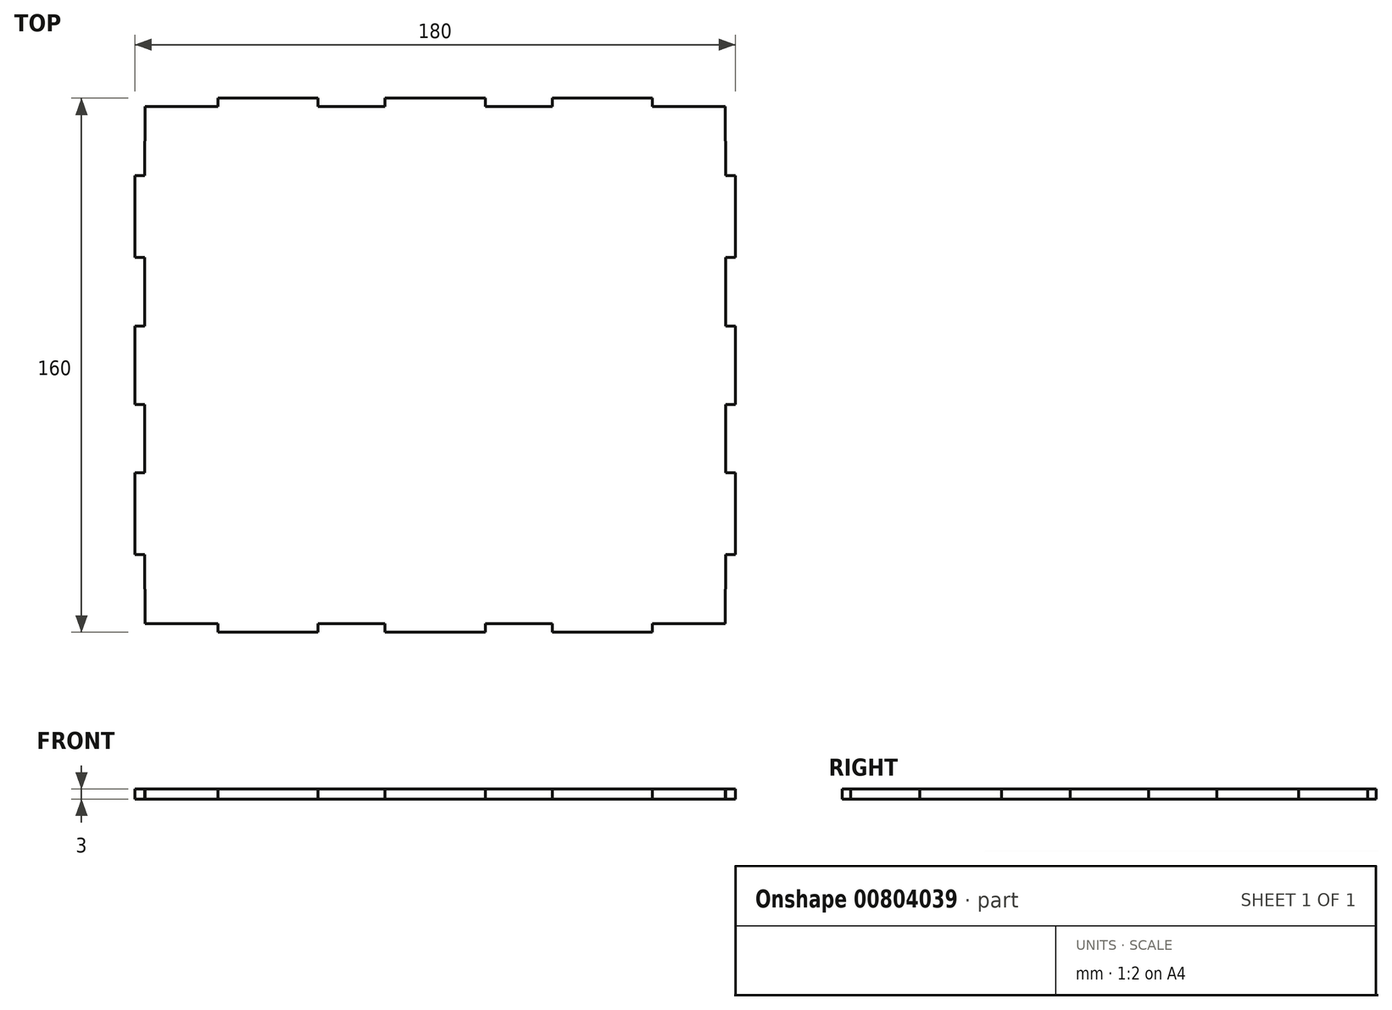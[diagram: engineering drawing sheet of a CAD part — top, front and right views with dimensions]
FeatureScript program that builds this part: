
annotation { "Feature Type Name" : "Feature", "Feature Type Description" : "" }
export const myFeature = defineFeature(function(context is Context, id is Id, definition is map)
    precondition{}
    {
        {
            var Q0;
            Q0=qCreatedBy(makeId("Top.planeOp"),FACE);
            var sketch = newSketch(context, id + "F0", { "sketchPlane" : qUnion([Q0])});
            skPoint(sketch, "E0.middle", {"position": v(0, 0) * mm});
            skLineSegment(sketch, "E1", {"start": v(90, 44.5) * mm, "end": v(88.5, 44.5) * mm});
            skLineSegment(sketch, "E2.bottom", {"start": v(87, 56.75) * mm, "end": v(90, 56.75) * mm});
            skLineSegment(sketch, "E2.top", {"start": v(87, 32.25) * mm, "end": v(90, 32.25) * mm});
            skLineSegment(sketch, "E2.right", {"start": v(90, 56.75) * mm, "end": v(90, 32.25) * mm});
            skPoint(sketch, "E2.middle", {"position": v(88.5, 44.5) * mm});
            skLineSegment(sketch, "E3.MirrorCS", {"start": v(87, -56.75) * mm, "end": v(90, -56.75) * mm});
            skLineSegment(sketch, "E4.MirrorCS", {"start": v(90, -56.75) * mm, "end": v(90, -32.25) * mm});
            skLineSegment(sketch, "E5.MirrorCS", {"start": v(87, -32.25) * mm, "end": v(90, -32.25) * mm});
            skLineSegment(sketch, "E6.bottom", {"start": v(90, 32.25) * mm, "end": v(87, 32.25) * mm});
            skLineSegment(sketch, "E6.top", {"start": v(90, 11.75) * mm, "end": v(87, 11.75) * mm});
            skLineSegment(sketch, "E6.right", {"start": v(87, 32.25) * mm, "end": v(87, 11.75) * mm});
            skPoint(sketch, "E6.middle", {"position": v(88.5, 22) * mm});
            skLineSegment(sketch, "E7.MirrorCS", {"start": v(87, -32.25) * mm, "end": v(87, -11.75) * mm});
            skLineSegment(sketch, "E8.MirrorCS", {"start": v(90, -11.75) * mm, "end": v(87, -11.75) * mm});
            skLineSegment(sketch, "E9", {"start": v(90, 11.75) * mm, "end": v(90, -11.75) * mm});
            skLineSegment(sketch, "E10.MirrorCS", {"start": v(-90, 32.25) * mm, "end": v(-87, 32.25) * mm});
            skLineSegment(sketch, "E11.MirrorCS", {"start": v(-87, 32.25) * mm, "end": v(-90, 32.25) * mm});
            skLineSegment(sketch, "E12.MirrorCS", {"start": v(-87, -56.75) * mm, "end": v(-90, -56.75) * mm});
            skLineSegment(sketch, "E13.MirrorCS", {"start": v(-87, -32.25) * mm, "end": v(-90, -32.25) * mm});
            skLineSegment(sketch, "E14.MirrorCS", {"start": v(-90, -11.75) * mm, "end": v(-87, -11.75) * mm});
            skLineSegment(sketch, "E15.MirrorCS", {"start": v(-87, 56.75) * mm, "end": v(-90, 56.75) * mm});
            skLineSegment(sketch, "E16.MirrorCS", {"start": v(-90, 44.5) * mm, "end": v(-88.5, 44.5) * mm});
            skLineSegment(sketch, "E17.MirrorCS", {"start": v(-90, 11.75) * mm, "end": v(-87, 11.75) * mm});
            skPoint(sketch, "E18.MirrorP", {"position": v(-88.5, 44.5) * mm});
            skLineSegment(sketch, "E19.MirrorCS", {"start": v(-90, 11.75) * mm, "end": v(-90, -11.75) * mm});
            skLineSegment(sketch, "E20.MirrorCS", {"start": v(-90, -56.75) * mm, "end": v(-90, -32.25) * mm});
            skPoint(sketch, "E21.MirrorP", {"position": v(-88.5, 22) * mm});
            skLineSegment(sketch, "E22.MirrorCS", {"start": v(-87, 32.25) * mm, "end": v(-87, 11.75) * mm});
            skLineSegment(sketch, "E23.MirrorCS", {"start": v(-90, 56.75) * mm, "end": v(-90, 32.25) * mm});
            skLineSegment(sketch, "E24.MirrorCS", {"start": v(-87, -32.25) * mm, "end": v(-87, -11.75) * mm});
            skLineSegment(sketch, "E25", {"start": v(-50.12, -77.22) * mm, "end": v(-50.13, -78.72) * mm});
            skLineSegment(sketch, "E26.top", {"start": v(-65.13, -80) * mm, "end": v(-35.13, -80) * mm});
            skLineSegment(sketch, "E26.left", {"start": v(-65.13, -77.44) * mm, "end": v(-65.13, -80) * mm});
            skLineSegment(sketch, "E26.right", {"start": v(-35.13, -77.44) * mm, "end": v(-35.13, -80) * mm});
            skPoint(sketch, "E26.middle", {"position": v(-50.13, -78.72) * mm});
            skLineSegment(sketch, "E27.MirrorCS", {"start": v(65.13, -77.44) * mm, "end": v(65.13, -80) * mm});
            skLineSegment(sketch, "E28.MirrorCS", {"start": v(65.13, -80) * mm, "end": v(35.13, -80) * mm});
            skLineSegment(sketch, "E29.MirrorCS", {"start": v(35.13, -77.44) * mm, "end": v(35.13, -80) * mm});
            skLineSegment(sketch, "E30", {"start": v(-65.13, 77.44) * mm, "end": v(-86.88, 77.44) * mm});
            skLineSegment(sketch, "E31", {"start": v(-86.88, 77.44) * mm, "end": v(-87, 56.75) * mm});
            skLineSegment(sketch, "E32.MirrorCS", {"start": v(65.13, 77.44) * mm, "end": v(86.88, 77.44) * mm});
            skLineSegment(sketch, "E33.MirrorCS", {"start": v(86.88, 77.44) * mm, "end": v(87, 56.75) * mm});
            skLineSegment(sketch, "E34.MirrorCS", {"start": v(-65.13, -77.44) * mm, "end": v(-86.88, -77.44) * mm});
            skLineSegment(sketch, "E35.MirrorCS", {"start": v(-86.88, -77.44) * mm, "end": v(-87, -56.75) * mm});
            skLineSegment(sketch, "E36.MirrorCS", {"start": v(65.13, -77.44) * mm, "end": v(86.88, -77.44) * mm});
            skLineSegment(sketch, "E37.MirrorCS", {"start": v(86.88, -77.44) * mm, "end": v(87, -56.75) * mm});
            skPoint(sketch, "E38.endSnap0", {"position": v(0, -80) * mm});
            skLineSegment(sketch, "E39.top", {"start": v(-15, -80) * mm, "end": v(15, -80) * mm});
            skLineSegment(sketch, "E39.left", {"start": v(-15, -77.44) * mm, "end": v(-15, -80) * mm});
            skLineSegment(sketch, "E39.right", {"start": v(15, -77.44) * mm, "end": v(15, -80) * mm});
            skPoint(sketch, "E39.middle", {"position": v(0, -78.72) * mm});
            skLineSegment(sketch, "E40", {"start": v(-35.13, -77.44) * mm, "end": v(-15, -77.44) * mm});
            skLineSegment(sketch, "E41", {"start": v(15, -77.44) * mm, "end": v(35.13, -77.44) * mm});
            skLineSegment(sketch, "E42.MirrorCS", {"start": v(-15, 77.44) * mm, "end": v(-15, 80) * mm});
            skLineSegment(sketch, "E43.MirrorCS", {"start": v(15, 77.44) * mm, "end": v(15, 80) * mm});
            skLineSegment(sketch, "E44.MirrorCS", {"start": v(65.13, 77.44) * mm, "end": v(65.13, 80) * mm});
            skLineSegment(sketch, "E45.MirrorCS", {"start": v(-65.13, 77.44) * mm, "end": v(-65.13, 80) * mm});
            skLineSegment(sketch, "E46.MirrorCS", {"start": v(-35.13, 77.44) * mm, "end": v(-35.13, 80) * mm});
            skLineSegment(sketch, "E47.MirrorCS", {"start": v(-50.12, 77.22) * mm, "end": v(-50.13, 78.72) * mm});
            skLineSegment(sketch, "E48.MirrorCS", {"start": v(35.13, 77.44) * mm, "end": v(35.13, 80) * mm});
            skLineSegment(sketch, "E49.MirrorCS", {"start": v(-15, 80) * mm, "end": v(15, 80) * mm});
            skLineSegment(sketch, "E50.MirrorCS", {"start": v(-35.13, 77.44) * mm, "end": v(-15, 77.44) * mm});
            skLineSegment(sketch, "E51.MirrorCS", {"start": v(-65.13, 80) * mm, "end": v(-35.13, 80) * mm});
            skLineSegment(sketch, "E52.MirrorCS", {"start": v(15, 77.44) * mm, "end": v(35.13, 77.44) * mm});
            skPoint(sketch, "E53.MirrorP", {"position": v(-50.13, 78.72) * mm});
            skPoint(sketch, "E54.MirrorP", {"position": v(0, 78.72) * mm});
            skLineSegment(sketch, "E55.MirrorCS", {"start": v(65.13, 80) * mm, "end": v(35.13, 80) * mm});
            skPoint(sketch, "E56.MirrorP", {"position": v(0, 80) * mm});
            skSolve(sketch);
        }
        {
            var Q0;
            {var subQ5=sQuery(id+"F0.wireOp",EDGE,"E2.bottom");Q0=makeQuery(id+"F0.imprint","IMPRINT",FACE,{"disambiguationData":[TD([[makeQuery(id+"F0.imprint","IMPRINT",EDGE,{"derivedFrom":subQ5}),-1.0]])]});}
            extrude(context, id + "F1", {"entities" : qUnion([Q0]), "depth" : 3 * mm, "offsetDistance" : 25 * mm});
        }
    });
